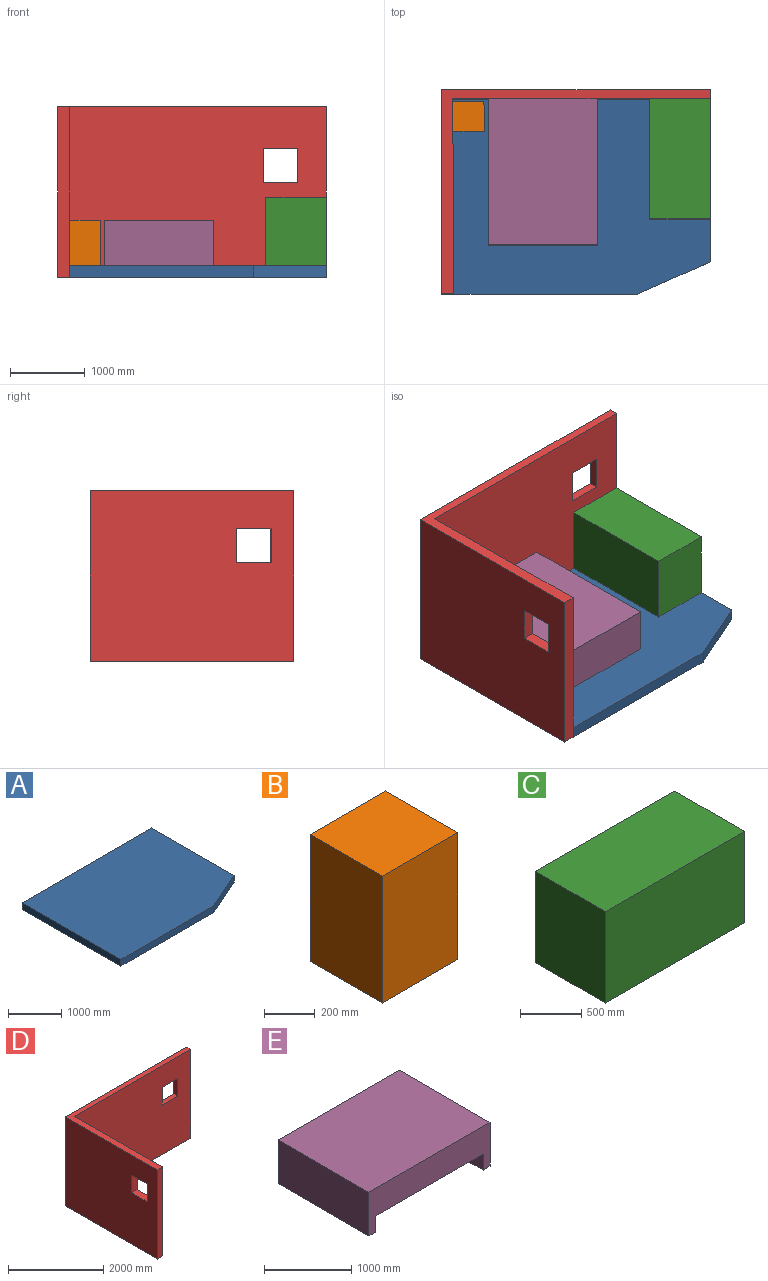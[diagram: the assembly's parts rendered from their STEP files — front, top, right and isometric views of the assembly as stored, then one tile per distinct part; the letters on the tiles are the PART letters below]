
ASSEMBLY  parts=5 mates=11
PART A: 7 faces, bbox 3454.4x2616.1x152.4 mm
  f0: plane 3454.4x152.4mm, normal (0,1,0), area 526450.6mm2, adj f1,f4,f5,f6
  f1: plane 2616.15x152.4mm, normal (-1,-0.01,0), area 398708.9mm2, adj f0,f2,f5,f6
  f2: plane 2463.8x152.4mm, normal (0,-1,0), area 375483.1mm2, adj f1,f3,f5,f6
  f3: plane 974.2x431.75mm, normal (0.41,-0.91,0), area 162394.9mm2, adj f2,f4,f5,f6
  f4: plane 2184.4x152.4mm, normal (1,0,0), area 332902.6mm2, adj f0,f3,f5,f6
  f5: plane 3454.4x2616.15mm, normal (0,0,1), area 8805464.3mm2, adj f0,f1,f2,f3,f4
  f6: plane 3454.4x2616.15mm, normal (0,0,-1), area 8805464.3mm2, adj f0,f1,f2,f3,f4
PART B: 6 faces, bbox 419.1x400.1x609.6 mm
  f0: plane 609.6x419.1mm, normal (0,1,0), area 255483.4mm2, adj f1,f3,f4,f5
  f1: plane 609.6x400.05mm, normal (-1,0,0), area 243870.5mm2, adj f0,f2,f4,f5
  f2: plane 609.6x419.1mm, normal (0,-1,0), area 255483.4mm2, adj f1,f3,f4,f5
  f3: plane 609.6x400.05mm, normal (1,0,0), area 243870.5mm2, adj f0,f2,f4,f5
  f4: plane 419.1x400.05mm, normal (0,0,1), area 167661mm2, adj f0,f1,f2,f3
  f5: plane 419.1x400.05mm, normal (0,0,-1), area 167661mm2, adj f0,f1,f2,f3
PART C: 6 faces, bbox 1609.7x809.6x914.4 mm
  f0: plane 1609.73x914.4mm, normal (0,1,0), area 1471932.5mm2, adj f1,f3,f4,f5
  f1: plane 914.4x809.63mm, normal (-1,0,0), area 740321.1mm2, adj f0,f2,f4,f5
  f2: plane 1609.73x914.4mm, normal (0,-1,0), area 1471932.5mm2, adj f1,f3,f4,f5
  f3: plane 914.4x809.63mm, normal (1,0,0), area 740321.1mm2, adj f0,f2,f4,f5
  f4: plane 1609.73x809.63mm, normal (0,0,1), area 1303273.6mm2, adj f0,f1,f2,f3
  f5: plane 1609.73x809.63mm, normal (0,0,-1), area 1303273.6mm2, adj f0,f1,f2,f3
PART D: 16 faces, bbox 3601.6x2734.4x2286 mm
  f0: plane 3454.4x2286mm, normal (0,-1,0), area 7687726.6mm2, adj f2,f4,f6,f7,f12,f13,f14,f15
  f1: plane 3601.56x2286mm, normal (0,1,0), area 8024126.1mm2, adj f3,f4,f6,f7,f12,f13,f14,f15
  f2: plane 2616.15x2286mm, normal (1,0.01,0), area 5771601.4mm2, adj f0,f5,f6,f7,f8,f9,f10,f11
  f3: plane 2734.36x2286mm, normal (-1,0,0), area 6041700.3mm2, adj f1,f5,f6,f7,f8,f9,f10,f11
  f4: plane 2286x118.21mm, normal (1,0,0), area 270220.6mm2, adj f0,f1,f6,f7
  f5: plane 2286x163.56mm, normal (0,-1,0), area 373894.6mm2, adj f2,f3,f6,f7
  f6: plane 3601.56x2734.36mm, normal (0,0,1), area 832166.4mm2, adj f0,f1,f2,f3,f4,f5
  f7: plane 3601.56x2734.36mm, normal (0,0,-1), area 832166.4mm2, adj f0,f1,f2,f3,f4,f5
  f8: plane 458.2x161.62mm, normal (0,0,-1), area 73240.7mm2, adj f2,f3,f9,f11
  f9: plane 457.2x161.62mm, normal (-0.01,1,0), area 73896mm2, adj f2,f3,f8,f10
  f10: plane 458.2x161.62mm, normal (0,0,1), area 73240.7mm2, adj f2,f3,f9,f11
  f11: plane 457.2x158.76mm, normal (0.01,-1,0), area 72585.4mm2, adj f2,f3,f8,f10
  f12: plane 457.2x118.21mm, normal (0,0,-1), area 54044.1mm2, adj f0,f1,f13,f15
  f13: plane 457.2x118.21mm, normal (1,0,0), area 54044.1mm2, adj f0,f1,f12,f14
  f14: plane 457.2x118.21mm, normal (0,0,1), area 54044.1mm2, adj f0,f1,f13,f15
  f15: plane 457.2x118.21mm, normal (-1,0,0), area 54044.1mm2, adj f0,f1,f12,f14
PART E: 10 faces, bbox 1959x1470x609.6 mm
  f0: plane 1470.03x112.18mm, normal (0,0,-1), area 164912.7mm2, adj f1,f3,f4,f8
  f1: plane 1958.98x609.6mm, normal (0,1,0), area 803937.6mm2, adj f0,f2,f4,f5,f6,f7,f8,f9
  f2: plane 1470.03x609.6mm, normal (-1,0,0), area 896127.2mm2, adj f1,f3,f5,f6
  f3: plane 1958.98x609.6mm, normal (0,-1,0), area 803937.6mm2, adj f0,f2,f4,f5,f6,f7,f8,f9
  f4: plane 1470.03x609.6mm, normal (1,0,0), area 896127.2mm2, adj f0,f1,f3,f5
  f5: plane 1958.98x1470.03mm, normal (0,0,1), area 2879742.2mm2, adj f1,f2,f3,f4
  f6: plane 1470.03x106.89mm, normal (0,0,-1), area 157133mm2, adj f1,f2,f3,f7
  f7: plane 1470.03x224.3mm, normal (1,0,0), area 329721.5mm2, adj f1,f3,f6,f9
  f8: plane 1470.03x224.3mm, normal (-1,0,0), area 329721.5mm2, adj f0,f1,f3,f9
  f9: plane 1739.9x1470.03mm, normal (0,0,-1), area 2557696.5mm2, adj f1,f3,f7,f8
PLACE A t=(1932.76,-601.32,-1175.4)mm
PLACE B rot(axis=(0,0,1),0.4deg) t=(428.08,102.51,-1023)mm
PLACE C rot(axis=(0,0,-1),90deg) t=(3135.73,-472.18,-1023)mm
PLACE D t=(1932.76,-601.32,-1175.4)mm
PLACE E rot(axis=(0,0,-1),90deg) t=(1098.12,-632.31,-1023)mm
MATE planar A.f5 <-> E.f6  axis (0,0,1) through (1915.39,-937.54,-1023)mm
MATE planar C.f5 <-> A.f5  axis (0,0,-1) through (3671.89,-463.19,-1023)mm
MATE planar E.f2 <-> D.f0  axis (0,1,0) through (1428.92,341.67,-718.2)mm
MATE planar C.f0 <-> D.f4  axis (1,0,0) through (3671.89,-463.19,-565.8)mm
MATE planar A.f6 <-> D.f7  axis (0,0,-1) through (1915.39,-937.54,-1175.4)mm
MATE planar A.f0 <-> D.f0  axis (0,1,0) through (1944.69,341.67,-1099.2)mm
MATE parallel C.f3 <-> D.f0  axis (0,-1,0) through (3671.89,-1268.05,-565.8)mm
MATE planar C.f1 <-> D.f0  axis (0,1,0) through (3267.07,341.67,-108.6)mm
MATE planar A.f4 <-> D.f4  axis (1,0,0) through (3671.89,-750.53,-1099.2)mm
MATE planar B.f5 <-> A.f5  axis (0,0,-1) through (428.5,108.97,-1023)mm
MATE planar B.f1 <-> D.f2  axis (-1,-0.01,0) through (218.95,107.66,-718.2)mm
